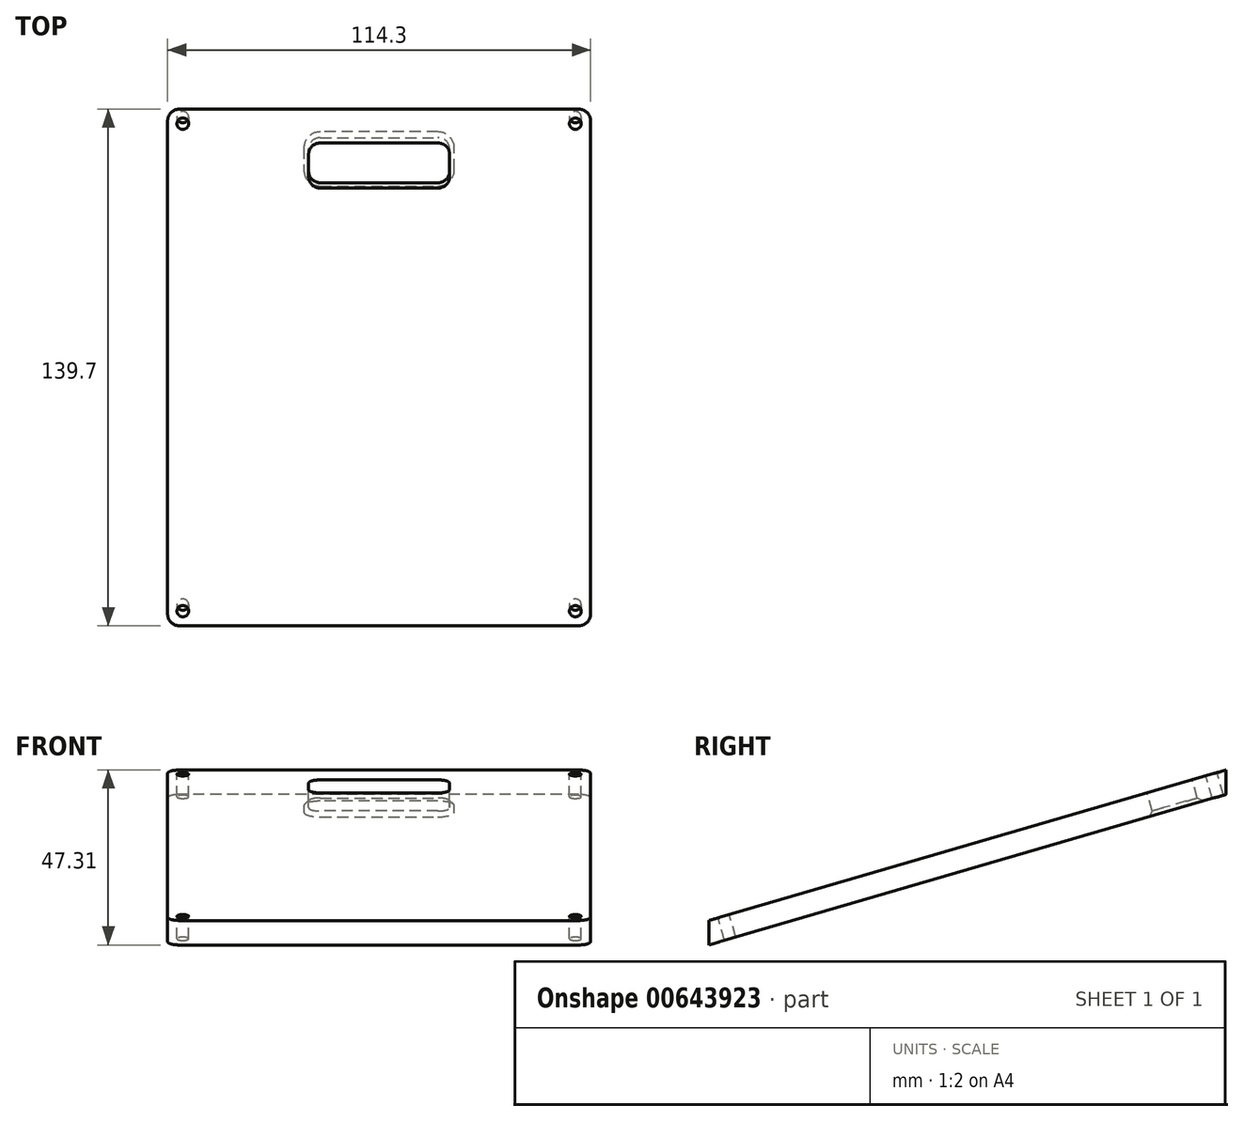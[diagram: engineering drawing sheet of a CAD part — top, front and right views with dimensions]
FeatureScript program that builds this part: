
annotation { "Feature Type Name" : "Feature", "Feature Type Description" : "" }
export const myFeature = defineFeature(function(context is Context, id is Id, definition is map)
    precondition{}
    {
        {
            var Q0;
            Q0=qCreatedBy(makeId("Right.planeOp"),FACE);
            var sketch = newSketch(context, id + "F0", { "sketchPlane" : qUnion([Q0])});
            skPoint(sketch, "E0", {"position": v(-69.06, 0) * mm});
            skPoint(sketch, "E1", {"position": v(70.64, 0) * mm});
            skLineSegment(sketch, "E2", {"start": v(-69.06, 0) * mm, "end": v(70.64, 40.7) * mm});
            skPoint(sketch, "E3", {"position": v(-69.06, 6.61) * mm});
            skPoint(sketch, "E4", {"position": v(70.64, 47.3) * mm});
            skPoint(sketch, "E5", {"position": v(70.64, 40.7) * mm});
            skLineSegment(sketch, "E6", {"start": v(-69.06, 6.61) * mm, "end": v(70.64, 47.3) * mm});
            skLineSegment(sketch, "E7", {"start": v(70.64, 40.7) * mm, "end": v(70.64, 47.3) * mm});
            skLineSegment(sketch, "E8", {"start": v(-69.06, 0) * mm, "end": v(-69.06, 6.61) * mm});
            skLineSegment(sketch, "E9", {"start": v(-69.06, 0) * mm, "end": v(70.64, 0) * mm, "construction": true});
            skSolve(sketch);
        }
        {
            var Q0;
            Q0=makeQuery(id+"F0.imprint","IMPRINT",FACE,{"disambiguationData":[TD([[makeQuery(id+"F0.imprint","IMPRINT",EDGE,{"derivedFrom":sQuery(id+"F0.wireOp",EDGE,"E2")}),1.0]])]});
            extrude(context, id + "F1", {"entities" : qUnion([Q0]), "depth" : 114.3 * mm, "offsetDistance" : 25.4 * mm});
        }
        {
            var Q0;
            Q0=makeQuery(id+"F1.opExtrude","SWEPT_FACE",FACE,{"disambiguationData":[OSD([sQuery(id+"F0.wireOp",EDGE,"E6")])]});
            var sketch = newSketch(context, id + "F2", { "sketchPlane" : qUnion([Q0])});
            skPoint(sketch, "E10", {"position": v(4.11, 81.05) * mm});
            skPoint(sketch, "E11", {"position": v(4.11, -64.46) * mm});
            skPoint(sketch, "E12", {"position": v(110.19, 81.05) * mm});
            skPoint(sketch, "E13", {"position": v(110.19, -64.46) * mm});
            skPoint(sketch, "E14", {"position": v(114.3, -60.34) * mm});
            skPoint(sketch, "E15", {"position": v(0, -60.34) * mm});
            skPoint(sketch, "E16", {"position": v(0, 76.94) * mm});
            skPoint(sketch, "E17", {"position": v(114.3, 76.94) * mm});
            skPoint(sketch, "E18", {"position": v(4.11, 76.94) * mm});
            skPoint(sketch, "E19", {"position": v(110.19, 76.94) * mm});
            skPoint(sketch, "E20", {"position": v(110.19, -60.34) * mm});
            skPoint(sketch, "E21", {"position": v(4.11, -60.34) * mm});
            skPoint(sketch, "E22", {"position": v(244.63, 90.64) * mm});
            skPoint(sketch, "E23", {"position": v(57.15, 81.05) * mm});
            skPoint(sketch, "E24", {"position": v(57.15, 71.53) * mm});
            skPoint(sketch, "E25", {"position": v(57.15, 65.18) * mm});
            skLineSegment(sketch, "E26.bottom", {"start": v(41.28, 71.53) * mm, "end": v(73.03, 71.53) * mm});
            skLineSegment(sketch, "E26.top", {"start": v(41.28, 58.83) * mm, "end": v(73.03, 58.83) * mm});
            skLineSegment(sketch, "E26.left", {"start": v(38.1, 68.35) * mm, "end": v(38.1, 62) * mm});
            skLineSegment(sketch, "E26.right", {"start": v(76.2, 68.35) * mm, "end": v(76.2, 62) * mm});
            skPoint(sketch, "E27.visualSharp", {"position": v(38.1, 71.53) * mm});
            skArc(sketch, "E27.filletArc", {"start": v(41.28, 71.53) * mm, "mid": v(39.03, 70.6) * mm, "end": v(38.1, 68.35) * mm});
            skPoint(sketch, "E28.visualSharp", {"position": v(76.2, 71.53) * mm});
            skArc(sketch, "E28.filletArc", {"start": v(76.2, 68.35) * mm, "mid": v(75.27, 70.6) * mm, "end": v(73.03, 71.53) * mm});
            skPoint(sketch, "E29.visualSharp", {"position": v(76.2, 58.83) * mm});
            skArc(sketch, "E29.filletArc", {"start": v(73.03, 58.83) * mm, "mid": v(75.27, 59.76) * mm, "end": v(76.2, 62) * mm});
            skPoint(sketch, "E30.visualSharp", {"position": v(38.1, 58.83) * mm});
            skArc(sketch, "E30.filletArc", {"start": v(38.1, 62) * mm, "mid": v(39.03, 59.76) * mm, "end": v(41.28, 58.83) * mm});
            skCircle(sketch, "E31", {"center": v(4.11, 76.94) * mm, "radius": 1.59 * mm});
            skCircle(sketch, "E32", {"center": v(110.19, 76.94) * mm, "radius": 1.59 * mm});
            skCircle(sketch, "E33", {"center": v(110.19, -60.34) * mm, "radius": 1.59 * mm});
            skCircle(sketch, "E34", {"center": v(4.11, -60.34) * mm, "radius": 1.59 * mm});
            skSolve(sketch);
        }
        {
            var Q0;
            Q0=makeQuery(id+"F2.imprint","IMPRINT",FACE,{"disambiguationData":[TD([[makeQuery(id+"F2.imprint","IMPRINT",EDGE,{"derivedFrom":sQuery(id+"F2.wireOp",EDGE,"E26.bottom")}),-1.0]])]});
            var Q1;
            Q1=makeQuery(id+"F2.imprint","IMPRINT",FACE,{"disambiguationData":[TD([[makeQuery(id+"F2.imprint","IMPRINT",EDGE,{"derivedFrom":sQuery(id+"F2.wireOp",EDGE,"E31")}),1.0]])]});
            var Q2;
            Q2=makeQuery(id+"F2.imprint","IMPRINT",FACE,{"disambiguationData":[TD([[makeQuery(id+"F2.imprint","IMPRINT",EDGE,{"derivedFrom":sQuery(id+"F2.wireOp",EDGE,"E32")}),1.0]])]});
            var Q3;
            Q3=makeQuery(id+"F2.imprint","IMPRINT",FACE,{"disambiguationData":[TD([[makeQuery(id+"F2.imprint","IMPRINT",EDGE,{"derivedFrom":sQuery(id+"F2.wireOp",EDGE,"E33")}),1.0]])]});
            var Q4;
            Q4=makeQuery(id+"F2.imprint","IMPRINT",FACE,{"disambiguationData":[TD([[makeQuery(id+"F2.imprint","IMPRINT",EDGE,{"derivedFrom":sQuery(id+"F2.wireOp",EDGE,"E34")}),1.0]])]});
            extrude(context, id + "F3", {"entities" : qUnion([Q0, Q1, Q2, Q3, Q4]), "operationType" : NewBodyOperationType.REMOVE, "oppositeDirection" : true, "depth" : 25.4 * mm, "offsetDistance" : 25.4 * mm});
        }
        {
            var Q0;
            Q0=makeQuery(id+"F3.boolean.opBoolean","COPY",EDGE,{"derivedFrom":makeQuery(id+"F3.opExtrude","CAP_EDGE",EDGE,{"disambiguationData":[OSD([sQuery(id+"F2.wireOp",EDGE,"E32")])],"isStart":true})});
            var Q1;
            Q1=makeQuery(id+"F3.boolean.opBoolean","COPY",EDGE,{"derivedFrom":makeQuery(id+"F3.opExtrude","CAP_EDGE",EDGE,{"disambiguationData":[OSD([sQuery(id+"F2.wireOp",EDGE,"E33")])],"isStart":true})});
            var Q2;
            Q2=makeQuery(id+"F3.boolean.opBoolean","COPY",EDGE,{"derivedFrom":makeQuery(id+"F3.opExtrude","CAP_EDGE",EDGE,{"disambiguationData":[OSD([sQuery(id+"F2.wireOp",EDGE,"E34")])],"isStart":true})});
            var Q3;
            Q3=makeQuery(id+"F3.boolean.opBoolean","COPY",EDGE,{"derivedFrom":makeQuery(id+"F3.opExtrude","CAP_EDGE",EDGE,{"disambiguationData":[OSD([sQuery(id+"F2.wireOp",EDGE,"E31")])],"isStart":true})});
            var Q4;
            Q4=makeQuery(id+"F3.boolean.opBoolean","COPY",EDGE,{"derivedFrom":makeQuery(id+"F3.opExtrude","CAP_EDGE",EDGE,{"disambiguationData":[OSD([sQuery(id+"F2.wireOp",EDGE,"E26.bottom")])],"isStart":true})});
            var Q5;
            Q5=makeQuery(id+"F3.boolean.opBoolean","COPY",EDGE,{"derivedFrom":makeQuery(id+"F3.opExtrude","CAP_EDGE",EDGE,{"disambiguationData":[OSD([sQuery(id+"F2.wireOp",EDGE,"E27.filletArc")])],"isStart":true})});
            var Q6;
            Q6=makeQuery(id+"F3.boolean.opBoolean","COPY",EDGE,{"derivedFrom":makeQuery(id+"F3.opExtrude","CAP_EDGE",EDGE,{"disambiguationData":[OSD([sQuery(id+"F2.wireOp",EDGE,"E26.left")])],"isStart":true})});
            var Q7;
            Q7=makeQuery(id+"F3.boolean.opBoolean","COPY",EDGE,{"derivedFrom":makeQuery(id+"F3.opExtrude","CAP_EDGE",EDGE,{"disambiguationData":[OSD([sQuery(id+"F2.wireOp",EDGE,"E30.filletArc")])],"isStart":true})});
            var Q8;
            Q8=makeQuery(id+"F3.boolean.opBoolean","COPY",EDGE,{"derivedFrom":makeQuery(id+"F3.opExtrude","CAP_EDGE",EDGE,{"disambiguationData":[OSD([sQuery(id+"F2.wireOp",EDGE,"E26.top")])],"isStart":true})});
            var Q9;
            Q9=makeQuery(id+"F3.boolean.opBoolean","COPY",EDGE,{"derivedFrom":makeQuery(id+"F3.opExtrude","CAP_EDGE",EDGE,{"disambiguationData":[OSD([sQuery(id+"F2.wireOp",EDGE,"E29.filletArc")])],"isStart":true})});
            var Q10;
            Q10=makeQuery(id+"F3.boolean.opBoolean","COPY",EDGE,{"derivedFrom":makeQuery(id+"F3.opExtrude","CAP_EDGE",EDGE,{"disambiguationData":[OSD([sQuery(id+"F2.wireOp",EDGE,"E26.right")])],"isStart":true})});
            var Q11;
            Q11=makeQuery(id+"F3.boolean.opBoolean","COPY",EDGE,{"derivedFrom":makeQuery(id+"F3.opExtrude","CAP_EDGE",EDGE,{"disambiguationData":[OSD([sQuery(id+"F2.wireOp",EDGE,"E28.filletArc")])],"isStart":true})});
            var Q12;
            Q12=makeQuery(id+"F3.boolean.opBoolean","INTERSECT",EDGE,{"derivedFrom":[makeQuery(id+"F1.opExtrude","SWEPT_FACE",FACE,{"disambiguationData":[OSD([sQuery(id+"F0.wireOp",EDGE,"E2")])]}),makeQuery(id+"F3.opExtrude","SWEPT_FACE",FACE,{"disambiguationData":[OSD([sQuery(id+"F2.wireOp",EDGE,"E26.top")])]})]});
            var Q13;
            Q13=makeQuery(id+"F3.boolean.opBoolean","INTERSECT",EDGE,{"derivedFrom":[makeQuery(id+"F1.opExtrude","SWEPT_FACE",FACE,{"disambiguationData":[OSD([sQuery(id+"F0.wireOp",EDGE,"E2")])]}),makeQuery(id+"F3.opExtrude","SWEPT_FACE",FACE,{"disambiguationData":[OSD([sQuery(id+"F2.wireOp",EDGE,"E29.filletArc")])]})]});
            chamfer(context, id + "F4", {"entities" : qUnion([Q0, Q1, Q2, Q3, Q4, Q5, Q6, Q7, Q8, Q9, Q10, Q11, Q12, Q13]), "width" : 1.27 * mm, "tangentPropagation" : true});
        }
        {
            var Q0;
            Q0=makeQuery(id+"F1.opExtrude","CAP_EDGE",EDGE,{"disambiguationData":[OSD([sQuery(id+"F0.wireOp",EDGE,"E8")])],"isStart":false});
            var Q1;
            Q1=makeQuery(id+"F1.opExtrude","CAP_EDGE",EDGE,{"disambiguationData":[OSD([sQuery(id+"F0.wireOp",EDGE,"E7")])],"isStart":false});
            var Q2;
            Q2=makeQuery(id+"F1.opExtrude","CAP_EDGE",EDGE,{"disambiguationData":[OSD([sQuery(id+"F0.wireOp",EDGE,"E8")])],"isStart":true});
            var Q3;
            Q3=makeQuery(id+"F1.opExtrude","CAP_EDGE",EDGE,{"disambiguationData":[OSD([sQuery(id+"F0.wireOp",EDGE,"E7")])],"isStart":true});
            fillet(context, id + "F5", {"entities" : qUnion([Q0, Q1, Q2, Q3]), "radius" : 3.17 * mm, "tangentPropagation" : true, "allowEdgeOverflow" : false});
        }
    });
